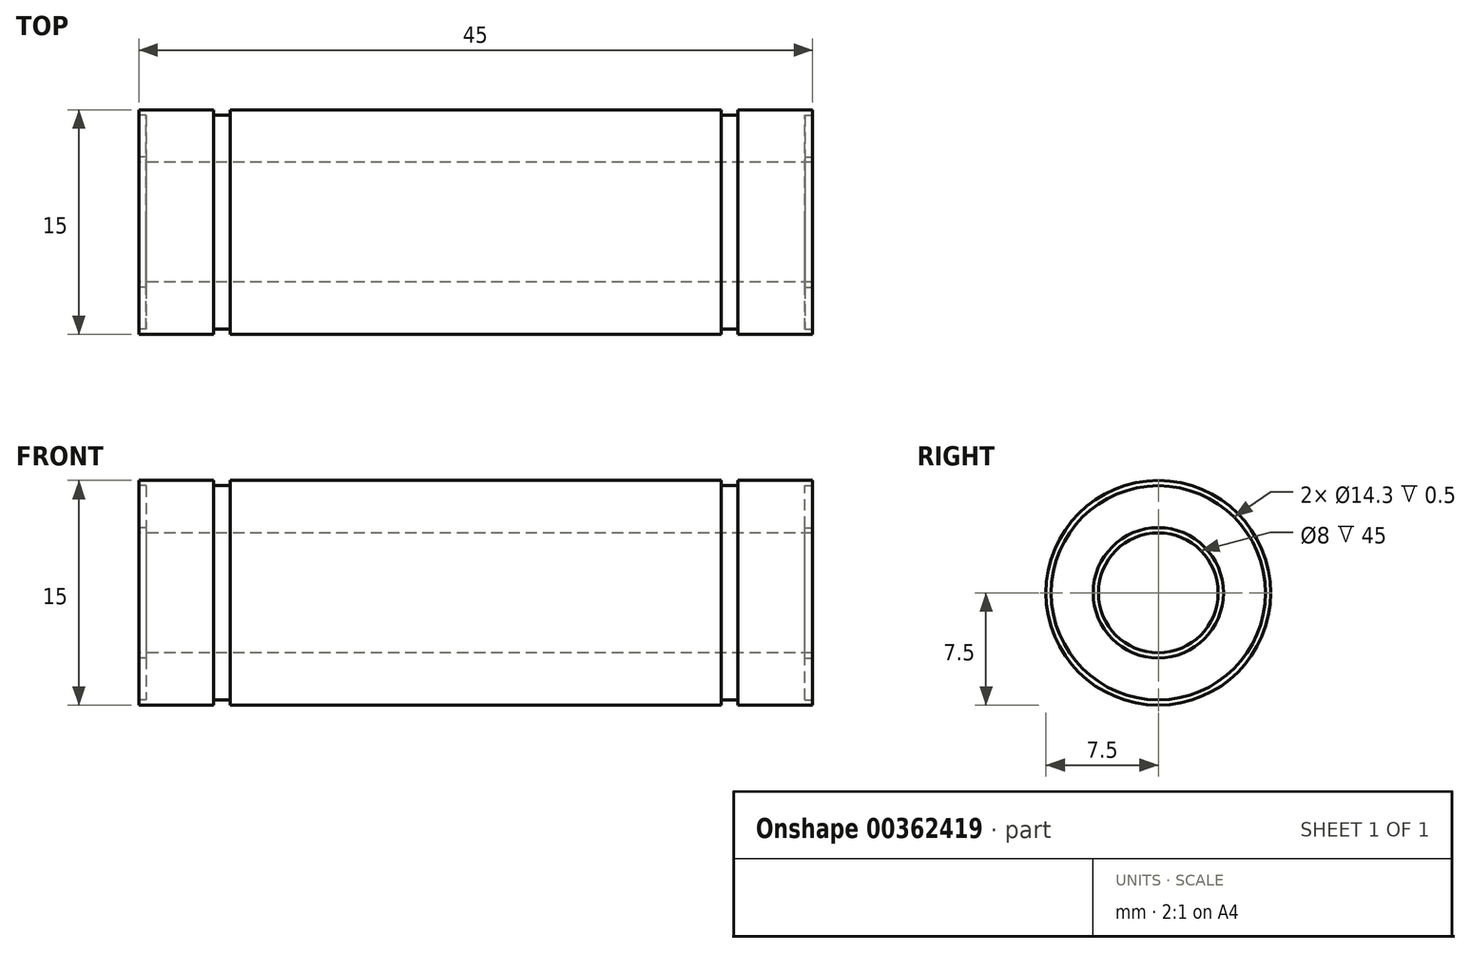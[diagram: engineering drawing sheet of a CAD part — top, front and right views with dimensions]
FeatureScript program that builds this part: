
annotation { "Feature Type Name" : "Feature", "Feature Type Description" : "" }
export const myFeature = defineFeature(function(context is Context, id is Id, definition is map)
    precondition{}
    {
        {
            var Q0;
            Q0=qCreatedBy(makeId("Right.planeOp"),FACE);
            var sketch = newSketch(context, id + "F0", { "sketchPlane" : qUnion([Q0])});
            skCircle(sketch, "E0", {"center": v(0, 0) * mm, "radius": 7.5 * mm});
            skCircle(sketch, "E1", {"center": v(0, 0) * mm, "radius": 4 * mm});
            skSolve(sketch);
        }
        {
            var Q0;
            Q0=makeQuery(id+"F0.imprint","IMPRINT",FACE,{"disambiguationData":[TD([[makeQuery(id+"F0.imprint","IMPRINT",EDGE,{"derivedFrom":sQuery(id+"F0.wireOp",EDGE,"E0")}),1.0]])]});
            extrude(context, id + "F1", {"entities" : qUnion([Q0]), "endBound" : BoundingType.SYMMETRIC, "depth" : 45 * mm});
        }
        {
            var Q0;
            Q0=qCreatedBy(makeId("Right.planeOp"),FACE);
            cPlane(context, id + "F2", {"entities" : qUnion([Q0]), "cplaneType" : CPlaneType.OFFSET, "offset" : 17.5 * mm, "width" : 150 * mm, "height" : 150 * mm});
        }
        {
            var Q0;
            Q0=qCreatedBy(makeId("Right.planeOp"),FACE);
            cPlane(context, id + "F3", {"entities" : qUnion([Q0]), "cplaneType" : CPlaneType.OFFSET, "offset" : 17.5 * mm, "oppositeDirection" : true, "width" : 150 * mm, "height" : 150 * mm});
        }
        {
            var Q0;
            Q0=qCreatedBy(id+"F3.planeOp",FACE);
            var sketch = newSketch(context, id + "F4", { "sketchPlane" : qUnion([Q0])});
            skCircle(sketch, "E2", {"center": v(0, 0) * mm, "radius": 7.15 * mm});
            skCircle(sketch, "E3", {"center": v(0, 0) * mm, "radius": 8 * mm});
            skSolve(sketch);
        }
        {
            var Q0;
            Q0=qSketchRegion(id+"F4",true);
            extrude(context, id + "F5", {"entities" : qUnion([Q0]), "operationType" : NewBodyOperationType.REMOVE, "depth" : 1.1 * mm});
        }
        {
            var Q0;
            Q0=qCreatedBy(id+"F2.planeOp",FACE);
            var sketch = newSketch(context, id + "F6", { "sketchPlane" : qUnion([Q0])});
            skCircle(sketch, "E4", {"center": v(0, 0) * mm, "radius": 7.15 * mm});
            skCircle(sketch, "E5", {"center": v(0, 0) * mm, "radius": 8 * mm});
            skSolve(sketch);
        }
        {
            var Q0;
            Q0=qSketchRegion(id+"F6",true);
            extrude(context, id + "F7", {"entities" : qUnion([Q0]), "operationType" : NewBodyOperationType.REMOVE, "oppositeDirection" : true, "depth" : 1.1 * mm});
        }
        {
            var Q0;
            Q0=makeQuery(id+"F1.opExtrude","CAP_FACE",FACE,{"disambiguationData":[OSD([sQuery(id+"F0.wireOp",EDGE,"E0"),sQuery(id+"F0.wireOp",EDGE,"E1")])],"isStart":false});
            var sketch = newSketch(context, id + "F8", { "sketchPlane" : qUnion([Q0])});
            skCircle(sketch, "E6", {"center": v(0, 0) * mm, "radius": 7.15 * mm});
            skCircle(sketch, "E7", {"center": v(0, 0) * mm, "radius": 4.35 * mm});
            skSolve(sketch);
        }
        {
            var Q0;
            Q0=qSketchRegion(id+"F8",true);
            extrude(context, id + "F9", {"entities" : qUnion([Q0]), "operationType" : NewBodyOperationType.REMOVE, "oppositeDirection" : true, "depth" : 0.5 * mm});
        }
        {
            var Q0;
            Q0=makeQuery(id+"F1.opExtrude","CAP_FACE",FACE,{"disambiguationData":[OSD([sQuery(id+"F0.wireOp",EDGE,"E0"),sQuery(id+"F0.wireOp",EDGE,"E1")])],"isStart":true});
            var sketch = newSketch(context, id + "F10", { "sketchPlane" : qUnion([Q0])});
            skSolve(sketch);
        }
        {
            var Q0;
            Q0=makeQuery(id+"F10.imprint","IMPRINT",FACE,{"disambiguationData":[TD([[makeQuery(id+"F10.imprint","IMPRINT",EDGE,{"derivedFrom":makeQuery(id+"F1.opExtrude","CAP_EDGE",EDGE,{"disambiguationData":[OSD([sQuery(id+"F0.wireOp",EDGE,"E0")])],"isStart":true})}),-1.0]])]});
            var sketch = newSketch(context, id + "F11", { "sketchPlane" : qUnion([Q0])});
            skCircle(sketch, "E8", {"center": v(0, 0) * mm, "radius": 4.35 * mm});
            skCircle(sketch, "E9", {"center": v(0, 0) * mm, "radius": 7.15 * mm});
            skSolve(sketch);
        }
        {
            var Q0;
            Q0=qSketchRegion(id+"F11",true);
            extrude(context, id + "F12", {"entities" : qUnion([Q0]), "operationType" : NewBodyOperationType.REMOVE, "oppositeDirection" : true, "depth" : 0.5 * mm});
        }
    });
